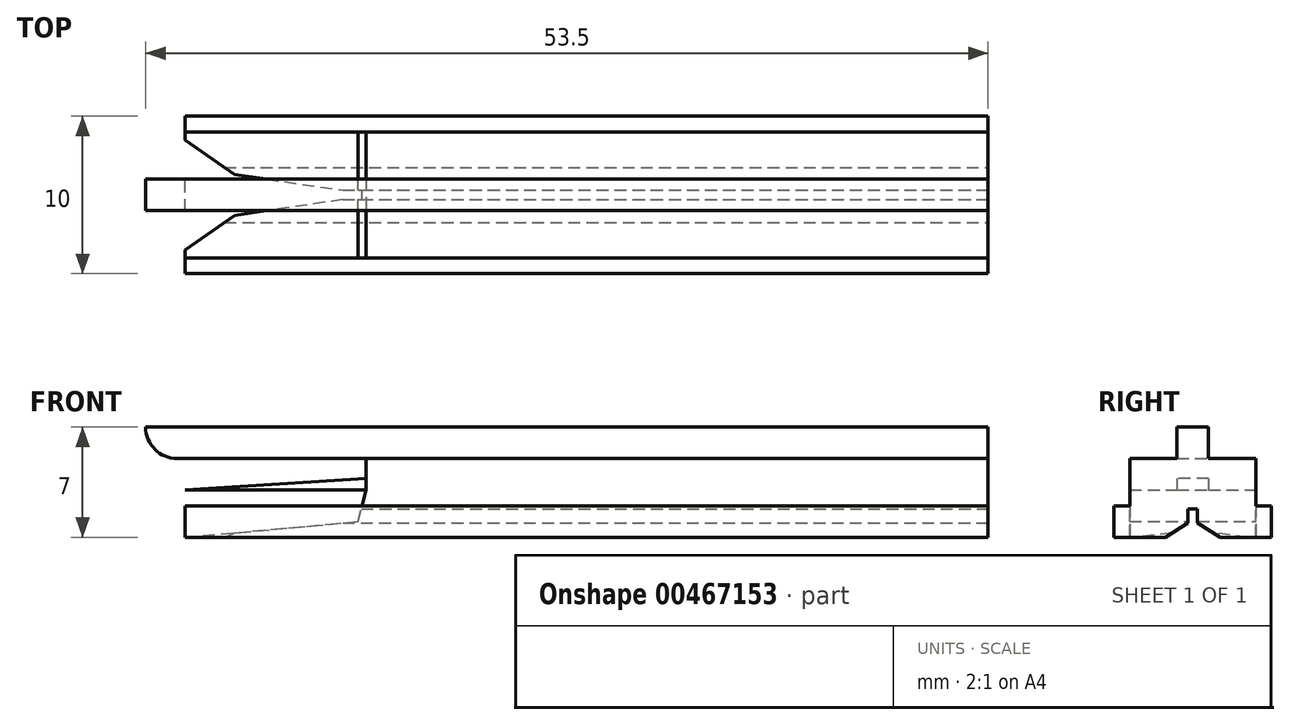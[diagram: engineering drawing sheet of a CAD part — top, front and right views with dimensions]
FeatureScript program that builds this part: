
annotation { "Feature Type Name" : "Feature", "Feature Type Description" : "" }
export const myFeature = defineFeature(function(context is Context, id is Id, definition is map)
    precondition{}
    {
        {
            var Q0;
            Q0=qCreatedBy(makeId("Front.planeOp"),FACE);
            var sketch = newSketch(context, id + "F0", { "sketchPlane" : qUnion([Q0])});
            skLineSegment(sketch, "E0.bottom", {"start": v(0, 5) * mm, "end": v(30, 5) * mm});
            skLineSegment(sketch, "E0.top", {"start": v(0, 0) * mm, "end": v(30, 0) * mm});
            skLineSegment(sketch, "E0.left", {"start": v(0, 5) * mm, "end": v(0, 0) * mm});
            skLineSegment(sketch, "E0.right", {"start": v(30, 5) * mm, "end": v(30, 0) * mm});
            skLineSegment(sketch, "E1", {"start": v(0, 0) * mm, "end": v(-21, 0) * mm});
            skLineSegment(sketch, "E2", {"start": v(-21, 0) * mm, "end": v(-10, 1) * mm});
            skLineSegment(sketch, "E3", {"start": v(-10, 1) * mm, "end": v(-9.5, 3) * mm});
            skLineSegment(sketch, "E4", {"start": v(-9.5, 3) * mm, "end": v(-9.5, 5) * mm});
            skLineSegment(sketch, "E5", {"start": v(-9.5, 5) * mm, "end": v(-9.5, 5) * mm});
            skLineSegment(sketch, "E6", {"start": v(-9.5, 5) * mm, "end": v(0, 5) * mm});
            skSolve(sketch);
        }
        {
            var Q0;
            Q0=makeQuery(id+"F0.imprint","IMPRINT",FACE,{"disambiguationData":[TD([[makeQuery(id+"F0.imprint","IMPRINT",EDGE,{"derivedFrom":sQuery(id+"F0.wireOp",EDGE,"E0.left")}),-1.0]])]});
            var Q1;
            Q1=makeQuery(id+"F0.imprint","IMPRINT",FACE,{"disambiguationData":[TD([[makeQuery(id+"F0.imprint","IMPRINT",EDGE,{"derivedFrom":sQuery(id+"F0.wireOp",EDGE,"E0.bottom")}),-1.0]])]});
            extrude(context, id + "F1", {"entities" : qUnion([Q0, Q1]), "depth" : 8 * mm});
        }
        {
            var Q0;
            Q0=makeQuery(id+"F1.opExtrude","SWEPT_FACE",FACE,{"disambiguationData":[OSD([sQuery(id+"F0.wireOp",EDGE,"E0.top"),sQuery(id+"F0.wireOp",EDGE,"E1")])]});
            var sketch = newSketch(context, id + "F2", { "sketchPlane" : qUnion([Q0])});
            skLineSegment(sketch, "E7", {"start": v(-21, 7.5) * mm, "end": v(-16, 4) * mm});
            skPoint(sketch, "E7.endSnap0", {"position": v(-21, 4) * mm});
            skLineSegment(sketch, "E8", {"start": v(-16, 4) * mm, "end": v(-21, 0.5) * mm});
            skLineSegment(sketch, "E9", {"start": v(-21, 0.5) * mm, "end": v(-21, 7.5) * mm});
            skSolve(sketch);
        }
        {
            var Q0;
            Q0=makeQuery(id+"F1.opExtrude","SWEPT_FACE",FACE,{"disambiguationData":[OSD([sQuery(id+"F0.wireOp",EDGE,"E0.right")])]});
            var sketch = newSketch(context, id + "F3", { "sketchPlane" : qUnion([Q0])});
            skLineSegment(sketch, "E10.bottom", {"start": v(-4.3, 1.8) * mm, "end": v(-3.7, 1.8) * mm});
            skLineSegment(sketch, "E10.top", {"start": v(-4.3, 0) * mm, "end": v(-3.7, 0) * mm});
            skLineSegment(sketch, "E10.left", {"start": v(-4.3, 1.8) * mm, "end": v(-4.3, 0) * mm});
            skLineSegment(sketch, "E10.right", {"start": v(-3.7, 1.8) * mm, "end": v(-3.7, 0) * mm});
            skLineSegment(sketch, "E11", {"start": v(-5.75, 0) * mm, "end": v(-4, 1.1) * mm});
            skLineSegment(sketch, "E12", {"start": v(-4, 1.1) * mm, "end": v(-2.25, 0) * mm});
            skLineSegment(sketch, "E13", {"start": v(-2.25, 0) * mm, "end": v(-5.75, 0) * mm});
            skSolve(sketch);
        }
        {
            var Q0;
            {var subQ5=sQuery(id+"F3.wireOp",EDGE,"E10.bottom");Q0=makeQuery(id+"F3.imprint","IMPRINT",FACE,{"disambiguationData":[TD([[makeQuery(id+"F3.imprint","IMPRINT",EDGE,{"derivedFrom":subQ5}),-1.0]])]});}
            var Q1;
            {var subQ1=sQuery(id+"F3.wireOp",EDGE,"E10.left");var subQ3=sQuery(id+"F3.wireOp",EDGE,"E11");var subQ4=makeQuery(id+"F3.imprint","INTERSECT",VERTEX,{"derivedFrom":[subQ1,subQ3]});Q1=makeQuery(id+"F3.imprint","IMPRINT",FACE,{"disambiguationData":[TD([[makeQuery(id+"F3.imprint","IMPRINT",EDGE,{"disambiguationData":[TD([[subQ4,-1.0]])],"derivedFrom":subQ1}),-1.0]])]});}
            var Q2;
            {var subQ1=sQuery(id+"F3.wireOp",EDGE,"E10.right");var subQ3=sQuery(id+"F3.wireOp",EDGE,"E12");var subQ4=makeQuery(id+"F3.imprint","INTERSECT",VERTEX,{"derivedFrom":[subQ1,subQ3]});Q2=makeQuery(id+"F3.imprint","IMPRINT",FACE,{"disambiguationData":[TD([[makeQuery(id+"F3.imprint","IMPRINT",EDGE,{"disambiguationData":[TD([[subQ4,-1.0]])],"derivedFrom":subQ1}),1.0]])]});}
            var Q3;
            {var subQ2=sQuery(id+"F3.wireOp",EDGE,"E10.top");Q3=makeQuery(id+"F3.imprint","IMPRINT",FACE,{"disambiguationData":[TD([[makeQuery(id+"F3.imprint","IMPRINT",EDGE,{"derivedFrom":subQ2}),1.0]])]});}
            extrude(context, id + "F4", {"entities" : qUnion([Q0, Q1, Q2, Q3]), "operationType" : NewBodyOperationType.REMOVE, "endBound" : BoundingType.THROUGH_ALL, "oppositeDirection" : true, "depth" : 25 * mm});
        }
        {
            var Q0;
            Q0=makeQuery(id+"F2.imprint","IMPRINT",FACE,{"disambiguationData":[TD([[makeQuery(id+"F2.imprint","IMPRINT",EDGE,{"derivedFrom":sQuery(id+"F2.wireOp",EDGE,"E7")}),-1.0]])]});
            extrude(context, id + "F5", {"entities" : qUnion([Q0]), "operationType" : NewBodyOperationType.REMOVE, "endBound" : BoundingType.THROUGH_ALL, "oppositeDirection" : true, "depth" : 25 * mm});
        }
        {
            var Q0;
            Q0=makeQuery(id+"F1.opExtrude","SWEPT_FACE",FACE,{"disambiguationData":[OSD([sQuery(id+"F0.wireOp",EDGE,"E0.right")])]});
            var sketch = newSketch(context, id + "F6", { "sketchPlane" : qUnion([Q0])});
            skLineSegment(sketch, "E14.bottom", {"start": v(-9, 2) * mm, "end": v(-8, 2) * mm});
            skLineSegment(sketch, "E14.top", {"start": v(-9, 0) * mm, "end": v(-8, 0) * mm});
            skLineSegment(sketch, "E14.left", {"start": v(-9, 2) * mm, "end": v(-9, 0) * mm});
            skLineSegment(sketch, "E14.right", {"start": v(-8, 2) * mm, "end": v(-8, 0) * mm});
            skLineSegment(sketch, "E15.bottom", {"start": v(0, 2) * mm, "end": v(1, 2) * mm});
            skLineSegment(sketch, "E15.top", {"start": v(0, 0) * mm, "end": v(1, 0) * mm});
            skLineSegment(sketch, "E15.left", {"start": v(0, 2) * mm, "end": v(0, 0) * mm});
            skLineSegment(sketch, "E15.right", {"start": v(1, 2) * mm, "end": v(1, 0) * mm});
            skSolve(sketch);
        }
        {
            var Q0;
            Q0=makeQuery(id+"F6.imprint","IMPRINT",FACE,{"disambiguationData":[TD([[makeQuery(id+"F6.imprint","IMPRINT",EDGE,{"derivedFrom":sQuery(id+"F6.wireOp",EDGE,"E14.bottom")}),-1.0]])]});
            var Q1;
            Q1=makeQuery(id+"F6.imprint","IMPRINT",FACE,{"disambiguationData":[TD([[makeQuery(id+"F6.imprint","IMPRINT",EDGE,{"derivedFrom":sQuery(id+"F6.wireOp",EDGE,"E15.bottom")}),-1.0]])]});
            var Q2;
            Q2=makeQuery(id+"F1.opExtrude","CAP_VERTEX",VERTEX,{"disambiguationData":[OSD([sQuery(id+"F0.wireOp",EDGE,"E1"),sQuery(id+"F0.wireOp",EDGE,"E2")])],"isStart":false});
            extrude(context, id + "F7", {"entities" : qUnion([Q0, Q1]), "operationType" : NewBodyOperationType.ADD, "endBound" : BoundingType.UP_TO_VERTEX, "oppositeDirection" : true, "endBoundEntityVertex" : qUnion([Q2]), "depth" : 25 * mm});
        }
        {
            var Q0;
            Q0=makeQuery(id+"F1.opExtrude","SWEPT_FACE",FACE,{"disambiguationData":[OSD([sQuery(id+"F0.wireOp",EDGE,"E4")])]});
            var sketch = newSketch(context, id + "F8", { "sketchPlane" : qUnion([Q0])});
            skLineSegment(sketch, "E16.bottom", {"start": v(3, 3.75) * mm, "end": v(5, 3.75) * mm});
            skLineSegment(sketch, "E16.top", {"start": v(3, 3) * mm, "end": v(5, 3) * mm});
            skLineSegment(sketch, "E16.left", {"start": v(3, 3.75) * mm, "end": v(3, 3) * mm});
            skLineSegment(sketch, "E16.right", {"start": v(5, 3.75) * mm, "end": v(5, 3) * mm});
            skSolve(sketch);
        }
        {
            var Q0;
            Q0=makeQuery(id+"F8.imprint","IMPRINT",FACE,{"disambiguationData":[TD([[makeQuery(id+"F8.imprint","IMPRINT",EDGE,{"derivedFrom":sQuery(id+"F8.wireOp",EDGE,"E16.bottom")}),-1.0]])]});
            extrude(context, id + "F9", {"entities" : qUnion([Q0]), "operationType" : NewBodyOperationType.ADD, "depth" : 11.5 * mm});
        }
        {
            var Q0;
            Q0=makeQuery(id+"F9.opExtrude","SWEPT_FACE",FACE,{"disambiguationData":[OSD([sQuery(id+"F8.wireOp",EDGE,"E16.right")])]});
            var sketch = newSketch(context, id + "F10", { "sketchPlane" : qUnion([Q0])});
            skLineSegment(sketch, "E17", {"start": v(-21, 3) * mm, "end": v(-9.5, 3.75) * mm});
            skLineSegment(sketch, "E18", {"start": v(-9.5, 3.75) * mm, "end": v(-21, 3.75) * mm});
            skLineSegment(sketch, "E19", {"start": v(-21, 3.75) * mm, "end": v(-21, 3) * mm});
            skSolve(sketch);
        }
        {
            var Q0;
            Q0=makeQuery(id+"F10.imprint","IMPRINT",FACE,{"disambiguationData":[TD([[makeQuery(id+"F10.imprint","IMPRINT",EDGE,{"derivedFrom":sQuery(id+"F10.wireOp",EDGE,"E17")}),1.0]])]});
            extrude(context, id + "F11", {"entities" : qUnion([Q0]), "operationType" : NewBodyOperationType.REMOVE, "endBound" : BoundingType.THROUGH_ALL, "oppositeDirection" : true, "depth" : 25 * mm});
        }
        {
            var Q0;
            Q0=makeQuery(id+"F1.opExtrude","SWEPT_FACE",FACE,{"disambiguationData":[OSD([sQuery(id+"F0.wireOp",EDGE,"E0.bottom"),sQuery(id+"F0.wireOp",EDGE,"E6")])]});
            var sketch = newSketch(context, id + "F12", { "sketchPlane" : qUnion([Q0])});
            skLineSegment(sketch, "E20.bottom", {"start": v(30, -3) * mm, "end": v(-23.5, -3) * mm});
            skLineSegment(sketch, "E20.top", {"start": v(30, -5) * mm, "end": v(-23.5, -5) * mm});
            skLineSegment(sketch, "E20.left", {"start": v(30, -3) * mm, "end": v(30, -5) * mm});
            skLineSegment(sketch, "E20.right", {"start": v(-23.5, -3) * mm, "end": v(-23.5, -5) * mm});
            skSolve(sketch);
        }
        {
            var Q0;
            {var subQ0=sQuery(id+"F12.wireOp",EDGE,"E20.left");Q0=makeQuery(id+"F12.imprint","IMPRINT",FACE,{"disambiguationData":[TD([[makeQuery(id+"F12.imprint","IMPRINT",EDGE,{"derivedFrom":subQ0}),1.0]])]});}
            var Q1;
            {var subQ0=sQuery(id+"F12.wireOp",EDGE,"E20.right");Q1=makeQuery(id+"F12.imprint","IMPRINT",FACE,{"disambiguationData":[TD([[makeQuery(id+"F12.imprint","IMPRINT",EDGE,{"derivedFrom":subQ0}),1.0]])]});}
            extrude(context, id + "F13", {"entities" : qUnion([Q0, Q1]), "operationType" : NewBodyOperationType.ADD, "depth" : 2 * mm});
        }
        {
            var Q0;
            Q0=makeQuery(id+"F13.opExtrude","CAP_EDGE",EDGE,{"disambiguationData":[OSD([sQuery(id+"F12.wireOp",EDGE,"E20.right")])],"isStart":true});
            fillet(context, id + "F14", {"entities" : qUnion([Q0]), "radius" : 2 * mm, "tangentPropagation" : true, "allowEdgeOverflow" : false});
        }
    });
